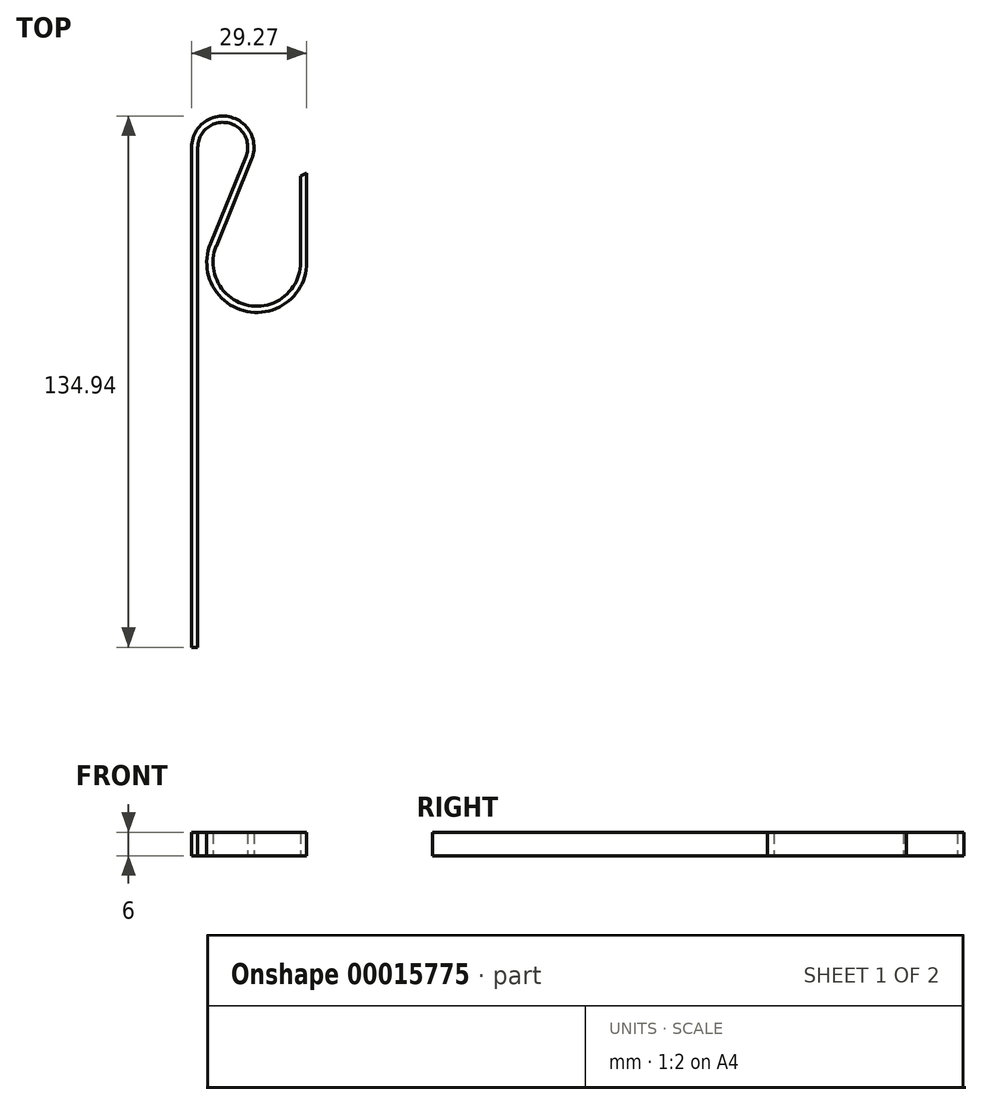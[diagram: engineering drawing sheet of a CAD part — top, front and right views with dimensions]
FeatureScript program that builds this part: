
annotation { "Feature Type Name" : "Feature", "Feature Type Description" : "" }
export const myFeature = defineFeature(function(context is Context, id is Id, definition is map)
    precondition{}
    {
        {
            var Q0;
            Q0=qCreatedBy(makeId("Top.planeOp"),FACE);
            var sketch = newSketch(context, id + "F0", { "sketchPlane" : qUnion([Q0])});
            skArc(sketch, "E0", {"start": v(5.88, -2.4) * mm, "mid": v(1.22, 6.23) * mm, "end": v(-6.35, 0) * mm});
            skLineSegment(sketch, "E1", {"start": v(0, 0) * mm, "end": v(-6.35, 0) * mm, "construction": true});
            skLineSegment(sketch, "E2", {"start": v(-6.35, 0) * mm, "end": v(-7.94, 0) * mm, "construction": true});
            skArc(sketch, "E3", {"start": v(7.35, -3) * mm, "mid": v(1.53, 7.79) * mm, "end": v(-7.94, 0) * mm});
            skLineSegment(sketch, "E4", {"start": v(0, 0) * mm, "end": v(0, -29.24) * mm, "construction": true});
            skLineSegment(sketch, "E5", {"start": v(0, -29.24) * mm, "end": v(8.63, -29.24) * mm, "construction": true});
            skLineSegment(sketch, "E6", {"start": v(5.88, -2.4) * mm, "end": v(-3.12, -24.44) * mm});
            skLineSegment(sketch, "E7", {"start": v(5.88, -2.4) * mm, "end": v(7.35, -3) * mm, "construction": true});
            skArc(sketch, "E8", {"start": v(-1.65, -25.04) * mm, "mid": v(6.5, -40.14) * mm, "end": v(19.75, -29.24) * mm});
            skArc(sketch, "E9", {"start": v(-3.12, -24.44) * mm, "mid": v(6.19, -41.7) * mm, "end": v(21.33, -29.24) * mm});
            skLineSegment(sketch, "E10", {"start": v(7.35, -3) * mm, "end": v(-1.65, -25.04) * mm});
            skLineSegment(sketch, "E11", {"start": v(-1.65, -25.04) * mm, "end": v(-3.12, -24.44) * mm, "construction": true});
            skLineSegment(sketch, "E12", {"start": v(-6.35, 0) * mm, "end": v(-6.35, -127) * mm});
            skLineSegment(sketch, "E13", {"start": v(-7.94, 0) * mm, "end": v(-7.94, -127) * mm});
            skLineSegment(sketch, "E14", {"start": v(8.63, -29.24) * mm, "end": v(19.75, -29.24) * mm, "construction": true});
            skLineSegment(sketch, "E15", {"start": v(21.33, -29.24) * mm, "end": v(19.75, -29.24) * mm, "construction": true});
            skLineSegment(sketch, "E16", {"start": v(19.75, -29.24) * mm, "end": v(19.75, -7.36) * mm});
            skLineSegment(sketch, "E17", {"start": v(21.33, -29.24) * mm, "end": v(21.33, -6.6) * mm});
            skLineSegment(sketch, "E18", {"start": v(19.75, -7.36) * mm, "end": v(21.33, -6.6) * mm});
            skLineSegment(sketch, "E19", {"start": v(-6.35, -127) * mm, "end": v(-7.94, -127) * mm});
            skSolve(sketch);
        }
        {
            var Q0;
            Q0 = qSketchRegion(id + "F0", true);
            extrude(context, id + "F1", {"entities" : qUnion([Q0]), "depth" : 6 * mm});
        }
    });
